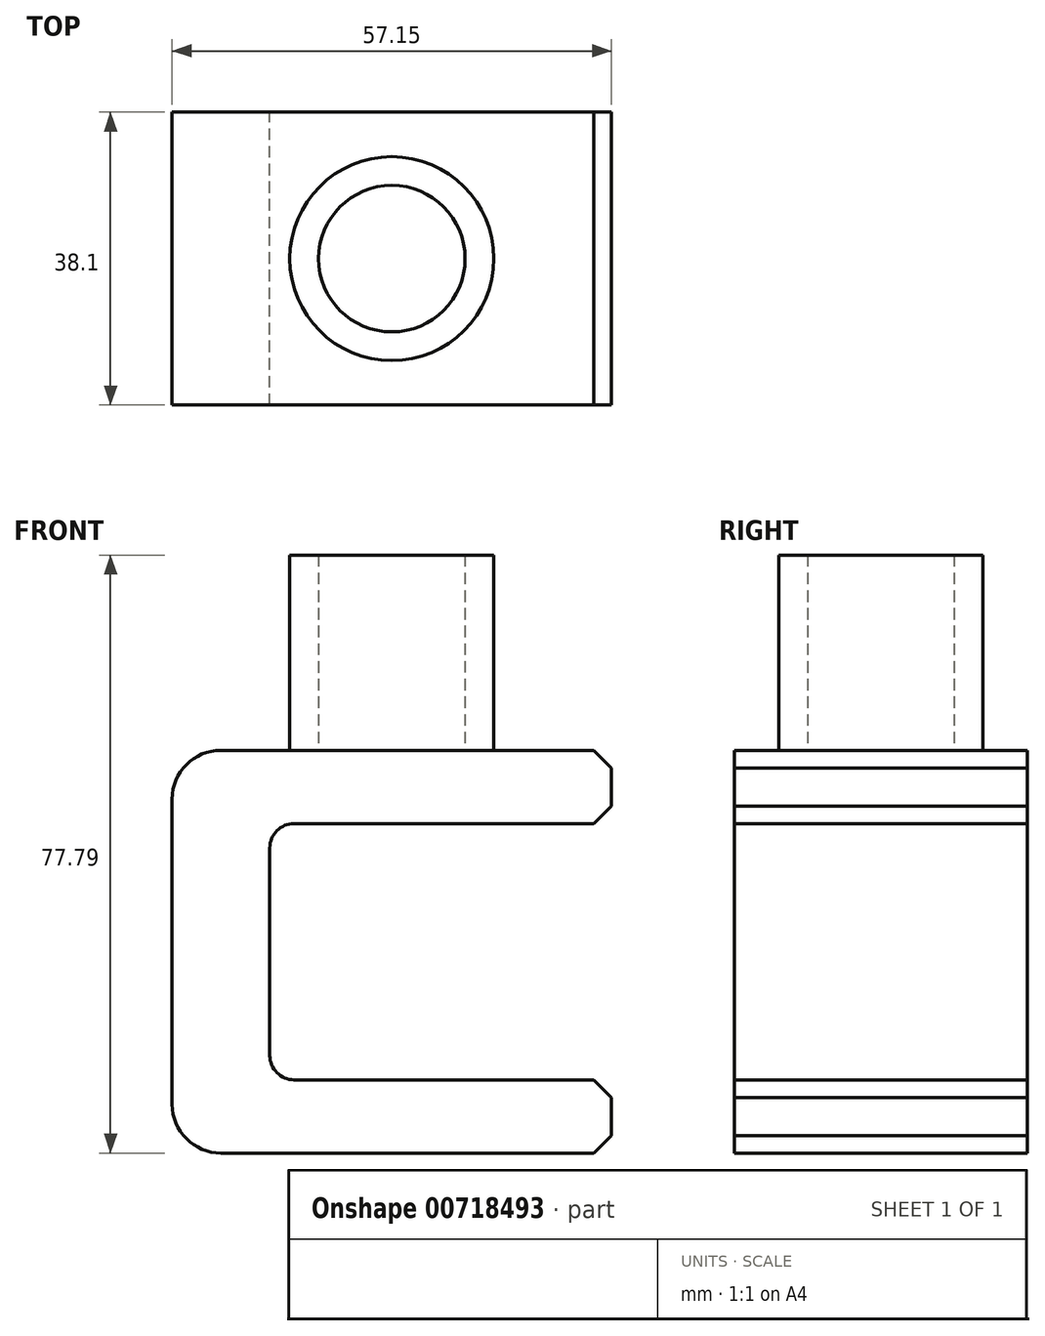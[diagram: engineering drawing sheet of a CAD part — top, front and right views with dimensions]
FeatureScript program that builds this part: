
annotation { "Feature Type Name" : "Feature", "Feature Type Description" : "" }
export const myFeature = defineFeature(function(context is Context, id is Id, definition is map)
    precondition{}
    {
        {
            var Q0;
            Q0=qCreatedBy(makeId("Front.planeOp"),FACE);
            var sketch = newSketch(context, id + "F0", { "sketchPlane" : qUnion([Q0])});
            skLineSegment(sketch, "E0", {"start": v(-22.22, 0) * mm, "end": v(0, 0) * mm});
            skLineSegment(sketch, "E1", {"start": v(0, 0) * mm, "end": v(26.29, 0) * mm});
            skLineSegment(sketch, "E2", {"start": v(28.58, -2.29) * mm, "end": v(28.58, -7.24) * mm});
            skLineSegment(sketch, "E3", {"start": v(26.29, -9.52) * mm, "end": v(-12.7, -9.53) * mm});
            skLineSegment(sketch, "E4", {"start": v(-15.87, -12.7) * mm, "end": v(-15.87, -39.69) * mm});
            skLineSegment(sketch, "E5", {"start": v(-12.7, -42.86) * mm, "end": v(26.29, -42.86) * mm});
            skLineSegment(sketch, "E6", {"start": v(28.57, -45.15) * mm, "end": v(28.57, -50.1) * mm});
            skLineSegment(sketch, "E7", {"start": v(26.29, -52.39) * mm, "end": v(-22.22, -52.39) * mm});
            skLineSegment(sketch, "E8", {"start": v(-28.57, -46.04) * mm, "end": v(-28.57, -6.35) * mm});
            skPoint(sketch, "E9.visualSharp", {"position": v(-15.87, -9.53) * mm});
            skArc(sketch, "E9.filletArc", {"start": v(-12.7, -9.53) * mm, "mid": v(-14.95, -10.45) * mm, "end": v(-15.87, -12.7) * mm});
            skPoint(sketch, "E10.visualSharp", {"position": v(-15.87, -42.86) * mm});
            skArc(sketch, "E10.filletArc", {"start": v(-15.87, -39.69) * mm, "mid": v(-14.95, -41.93) * mm, "end": v(-12.7, -42.86) * mm});
            skPoint(sketch, "E11.visualSharp", {"position": v(-28.57, 0) * mm});
            skArc(sketch, "E11.filletArc", {"start": v(-22.22, 0) * mm, "mid": v(-26.72, -1.86) * mm, "end": v(-28.57, -6.35) * mm});
            skPoint(sketch, "E12.visualSharp", {"position": v(-28.57, -52.39) * mm});
            skArc(sketch, "E12.filletArc", {"start": v(-28.57, -46.04) * mm, "mid": v(-26.72, -50.53) * mm, "end": v(-22.22, -52.39) * mm});
            skLineSegment(sketch, "E13", {"start": v(28.58, -2.29) * mm, "end": v(26.29, 0) * mm});
            skLineSegment(sketch, "E14", {"start": v(28.57, -7.24) * mm, "end": v(26.29, -9.53) * mm});
            skLineSegment(sketch, "E15", {"start": v(26.29, -42.86) * mm, "end": v(28.57, -45.15) * mm});
            skLineSegment(sketch, "E16", {"start": v(26.29, -52.39) * mm, "end": v(28.57, -50.1) * mm});
            skSolve(sketch);
        }
        {
            var Q0;
            Q0=qCreatedBy(makeId("Top.planeOp"),FACE);
            var sketch = newSketch(context, id + "F1", { "sketchPlane" : qUnion([Q0])});
            skCircle(sketch, "E17", {"center": v(0, 0) * mm, "radius": 13.27 * mm});
            skCircle(sketch, "E18", {"center": v(0, 0) * mm, "radius": 9.53 * mm});
            skSolve(sketch);
        }
        {
            var Q0;
            Q0=makeQuery(id+"F0.imprint","IMPRINT",FACE,{"disambiguationData":[TD([[makeQuery(id+"F0.imprint","IMPRINT",EDGE,{"derivedFrom":sQuery(id+"F0.wireOp",EDGE,"E0")}),-1.0]])]});
            extrude(context, id + "F2", {"entities" : qUnion([Q0]), "endBound" : BoundingType.SYMMETRIC, "depth" : 38.1 * mm, "offsetDistance" : 25.4 * mm});
        }
        {
            var Q0;
            Q0 = qSketchRegion(id + "F1", true);
            extrude(context, id + "F3", {"entities" : qUnion([Q0]), "operationType" : NewBodyOperationType.ADD, "depth" : 25.4 * mm, "offsetDistance" : 25.4 * mm});
        }
    });
